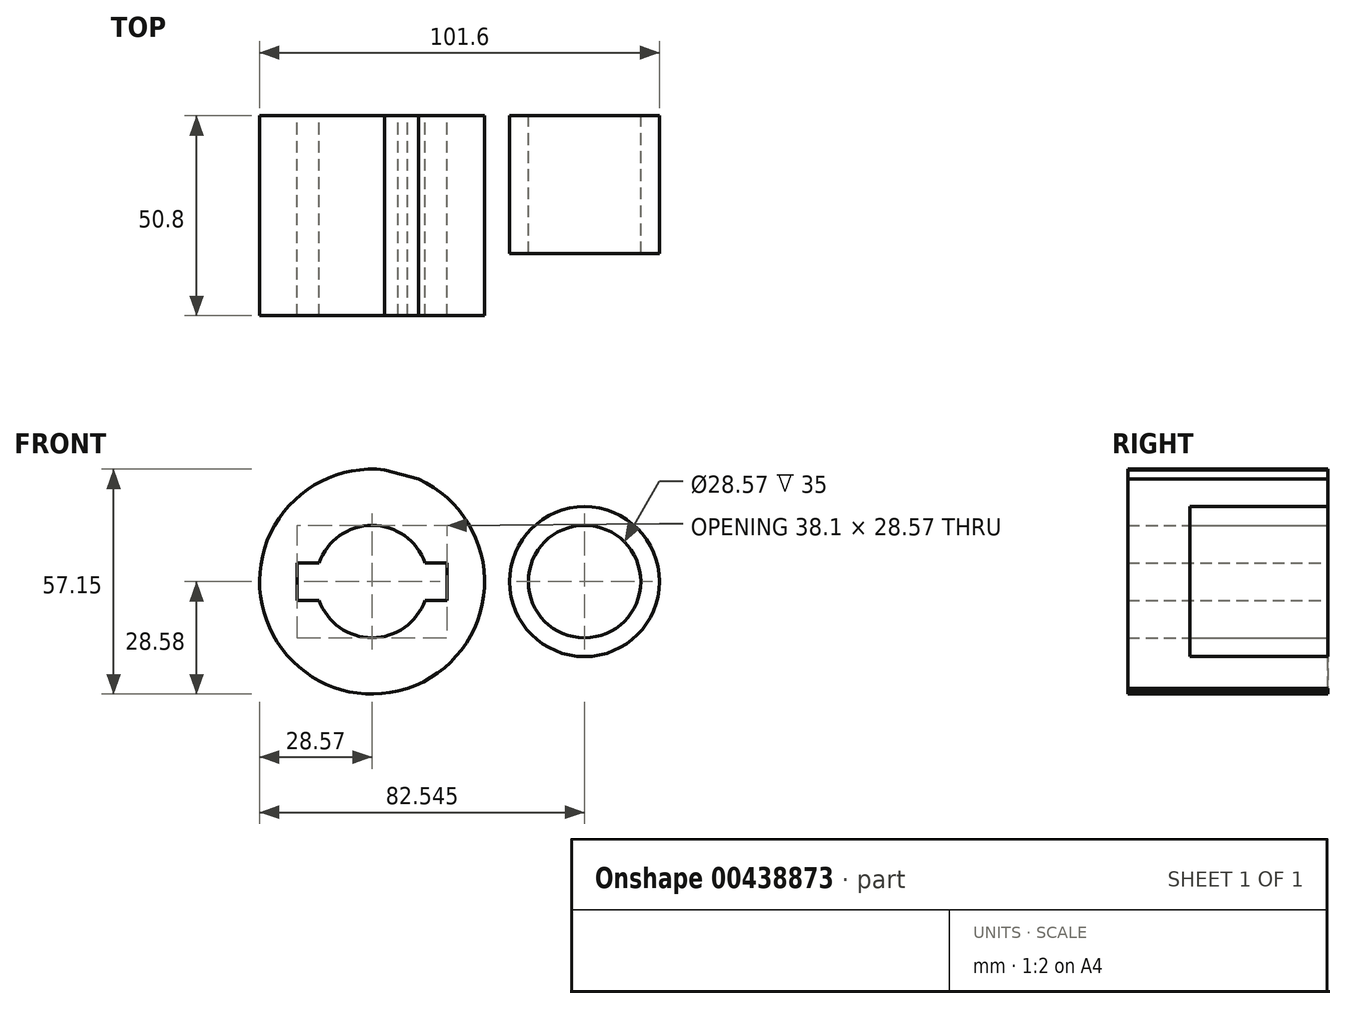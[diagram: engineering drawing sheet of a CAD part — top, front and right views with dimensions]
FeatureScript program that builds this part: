
annotation { "Feature Type Name" : "Feature", "Feature Type Description" : "" }
export const myFeature = defineFeature(function(context is Context, id is Id, definition is map)
    precondition{}
    {
        {
            var Q0;
            Q0=qCreatedBy(makeId("Front.planeOp"),FACE);
            var sketch = newSketch(context, id + "F0", { "sketchPlane" : qUnion([Q0])});
            skCircle(sketch, "E0", {"center": v(0, 0) * mm, "radius": 28.58 * mm});
            skCircle(sketch, "E1", {"center": v(53.98, 0) * mm, "radius": 19.05 * mm});
            skLineSegment(sketch, "E2", {"start": v(3.2, 28.4) * mm, "end": v(45.06, 16.84) * mm});
            skLineSegment(sketch, "E3", {"start": v(6.63, -27.8) * mm, "end": v(45.07, -16.84) * mm});
            skCircle(sketch, "E4", {"center": v(0, 0) * mm, "radius": 14.29 * mm});
            skCircle(sketch, "E5", {"center": v(53.98, 0) * mm, "radius": 14.29 * mm});
            skLineSegment(sketch, "E6.bottom", {"start": v(19.05, -4.76) * mm, "end": v(-19.05, -4.76) * mm});
            skLineSegment(sketch, "E6.top", {"start": v(19.05, 4.76) * mm, "end": v(-19.05, 4.76) * mm});
            skLineSegment(sketch, "E6.left", {"start": v(19.05, -4.76) * mm, "end": v(19.05, 4.76) * mm});
            skLineSegment(sketch, "E6.right", {"start": v(-19.05, -4.76) * mm, "end": v(-19.05, 4.76) * mm});
            skSolve(sketch);
        }
        {
            var Q0;
            {var subQ4=sQuery(id+"F0.wireOp",EDGE,"E6.left");Q0=makeQuery(id+"F0.imprint","IMPRINT",FACE,{"disambiguationData":[TD([[makeQuery(id+"F0.imprint","IMPRINT",EDGE,{"derivedFrom":subQ4}),-1.0]])]});}
            var Q1;
            {var subQ0=sQuery(id+"F0.wireOp",EDGE,"E2");var subQ1=sQuery(id+"F0.wireOp",EDGE,"E0");var subQ2=makeQuery(id+"F0.imprint","INTERSECT",VERTEX,{"disambiguationData":[OD(1.0)],"derivedFrom":[subQ1,subQ0]});Q1=makeQuery(id+"F0.imprint","IMPRINT",FACE,{"disambiguationData":[TD([[makeQuery(id+"F0.imprint","IMPRINT",EDGE,{"disambiguationData":[TD([[subQ2,1.0]])],"derivedFrom":subQ1}),-1.0]])]});}
            var Q2;
            Q2=makeQuery(id+"F0.imprint","IMPRINT",FACE,{"disambiguationData":[TD([[makeQuery(id+"F0.imprint","IMPRINT",EDGE,{"derivedFrom":sQuery(id+"F0.wireOp",EDGE,"E5")}),-1.0]])]});
            extrude(context, id + "F1", {"entities" : qUnion([Q0, Q1, Q2]), "depth" : 35 * mm});
        }
        {
            var Q0;
            {var subQ4=sQuery(id+"F0.wireOp",EDGE,"E6.left");Q0=makeQuery(id+"F0.imprint","IMPRINT",FACE,{"disambiguationData":[TD([[makeQuery(id+"F0.imprint","IMPRINT",EDGE,{"derivedFrom":subQ4}),-1.0]])]});}
            extrude(context, id + "F2", {"entities" : qUnion([Q0]), "operationType" : NewBodyOperationType.ADD, "depth" : 50.8 * mm});
        }
    });
